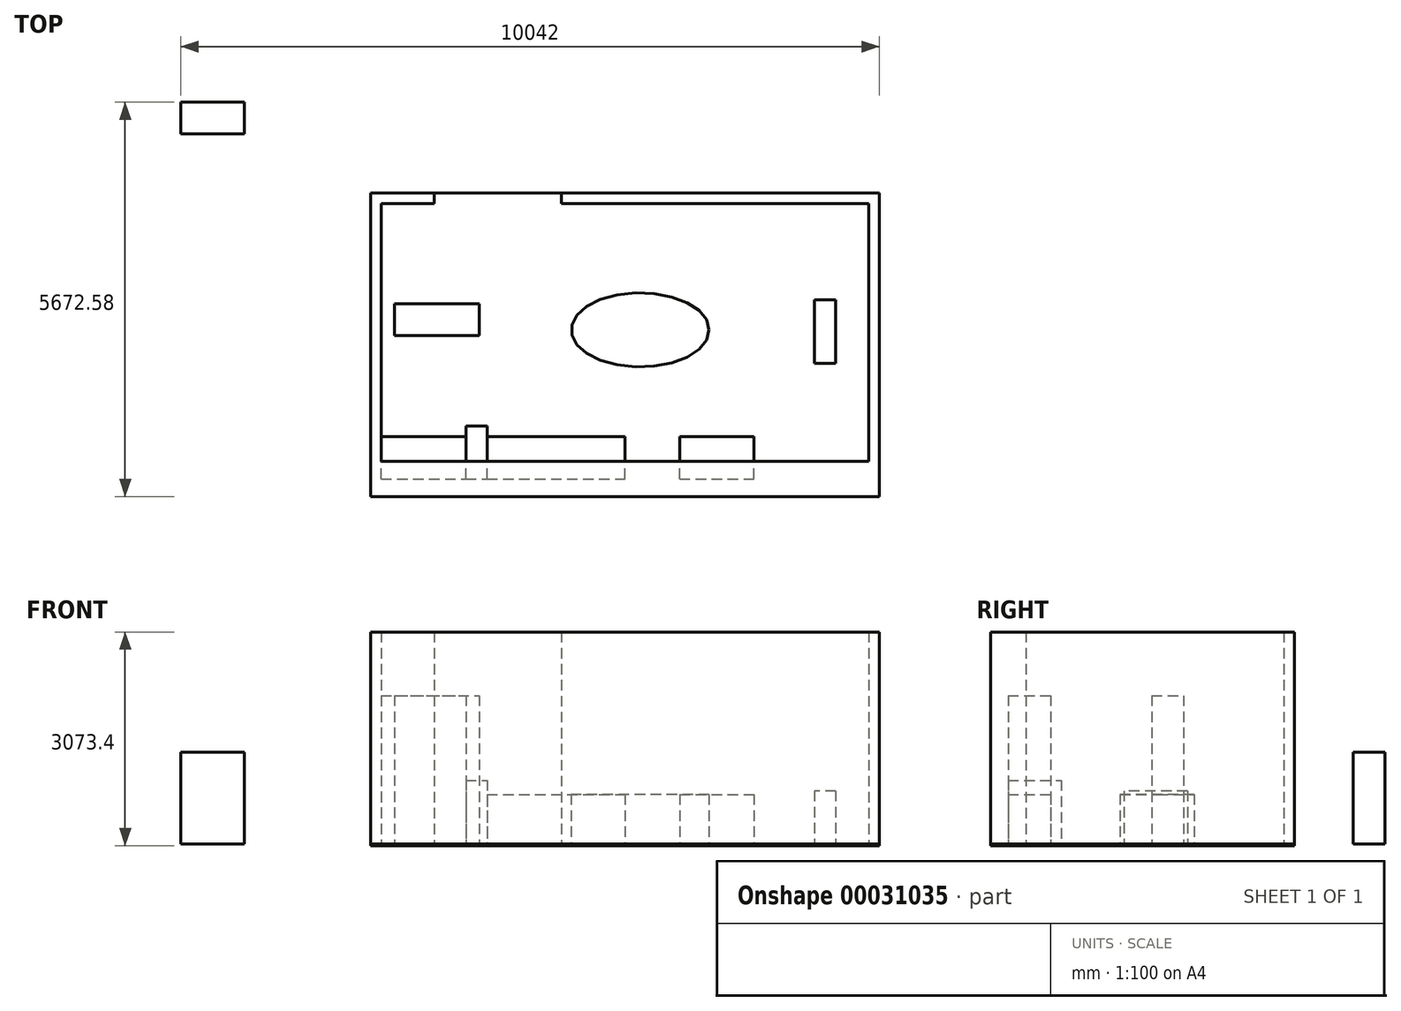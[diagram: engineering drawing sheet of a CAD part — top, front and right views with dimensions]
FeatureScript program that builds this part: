
annotation { "Feature Type Name" : "Feature", "Feature Type Description" : "" }
export const myFeature = defineFeature(function(context is Context, id is Id, definition is map)
    precondition{}
    {
        {
            var Q0;
            Q0=qCreatedBy(makeId("Top.planeOp"),FACE);
            var sketch = newSketch(context, id + "F0", { "sketchPlane" : qUnion([Q0])});
            skLineSegment(sketch, "E0.bottom", {"start": v(0, 0) * mm, "end": v(7010.4, 0) * mm, "construction": true});
            skLineSegment(sketch, "E0.top", {"start": v(0, 3962.4) * mm, "end": v(762, 3962.4) * mm});
            skLineSegment(sketch, "E0.left", {"start": v(0, 254) * mm, "end": v(0, 3962.4) * mm});
            skLineSegment(sketch, "E0.right", {"start": v(7010.4, 254) * mm, "end": v(7010.4, 3962.4) * mm});
            skLineSegment(sketch, "E1.bottom", {"start": v(-152.4, -254) * mm, "end": v(7162.8, -254) * mm});
            skLineSegment(sketch, "E1.top", {"start": v(-152.4, 4114.8) * mm, "end": v(762, 4114.8) * mm});
            skLineSegment(sketch, "E1.left", {"start": v(-152.4, -254) * mm, "end": v(-152.4, 4114.8) * mm});
            skLineSegment(sketch, "E1.right", {"start": v(7162.8, -254) * mm, "end": v(7162.8, 4114.8) * mm});
            skLineSegment(sketch, "E2.left", {"start": v(762, 3962.4) * mm, "end": v(762, 4114.8) * mm});
            skLineSegment(sketch, "E2.right", {"start": v(2590.8, 3962.4) * mm, "end": v(2590.8, 4114.8) * mm});
            skLineSegment(sketch, "E3.trimOffspring", {"start": v(2590.8, 3962.4) * mm, "end": v(7010.4, 3962.4) * mm});
            skLineSegment(sketch, "E4.trimOffspring", {"start": v(2590.8, 4114.8) * mm, "end": v(7162.8, 4114.8) * mm});
            skLineSegment(sketch, "E5", {"start": v(0, 254) * mm, "end": v(7010.4, 254) * mm});
            skSolve(sketch);
        }
        {
            var Q0;
            Q0 = qSketchRegion(id + "F0", true);
            extrude(context, id + "F1", {"entities" : qUnion([Q0]), "depth" : 3048 * mm});
        }
        {
            var Q0;
            Q0=makeQuery(id+"F1.opExtrude","CAP_FACE",FACE,{"disambiguationData":[OSD([sQuery(id+"F0.wireOp",EDGE,"E0.bottom"),sQuery(id+"F0.wireOp",EDGE,"E0.top"),sQuery(id+"F0.wireOp",EDGE,"E0.left"),sQuery(id+"F0.wireOp",EDGE,"E0.right"),sQuery(id+"F0.wireOp",EDGE,"E1.bottom"),sQuery(id+"F0.wireOp",EDGE,"E1.top"),sQuery(id+"F0.wireOp",EDGE,"E1.left"),sQuery(id+"F0.wireOp",EDGE,"E1.right"),sQuery(id+"F0.wireOp",EDGE,"E2.left"),sQuery(id+"F0.wireOp",EDGE,"E2.right"),sQuery(id+"F0.wireOp",EDGE,"E3.trimOffspring"),sQuery(id+"F0.wireOp",EDGE,"E4.trimOffspring")])],"isStart":true});
            var sketch = newSketch(context, id + "F2", { "sketchPlane" : qUnion([Q0])});
            skLineSegment(sketch, "E6.bottom", {"start": v(-152.4, 254) * mm, "end": v(7162.8, 254) * mm});
            skLineSegment(sketch, "E6.top", {"start": v(-152.4, -4114.8) * mm, "end": v(7162.8, -4114.8) * mm});
            skLineSegment(sketch, "E6.left", {"start": v(-152.4, 254) * mm, "end": v(-152.4, -4114.8) * mm});
            skLineSegment(sketch, "E6.right", {"start": v(7162.8, 254) * mm, "end": v(7162.8, -4114.8) * mm});
            skSolve(sketch);
        }
        {
            var Q0;
            Q0 = qSketchRegion(id + "F2", true);
            extrude(context, id + "F3", {"entities" : qUnion([Q0]), "depth" : 25.4 * mm});
        }
        {
            var Q0;
            Q0=makeQuery(id+"F3.opExtrude","CAP_FACE",FACE,{"disambiguationData":[OSD([sQuery(id+"F2.wireOp",EDGE,"E6.bottom"),sQuery(id+"F2.wireOp",EDGE,"E6.top"),sQuery(id+"F2.wireOp",EDGE,"E6.left"),sQuery(id+"F2.wireOp",EDGE,"E6.right")])],"isStart":true});
            var sketch = newSketch(context, id + "F4", { "sketchPlane" : qUnion([Q0])});
            skLineSegment(sketch, "E7.bottom", {"start": v(0, 0) * mm, "end": v(1219.2, 0) * mm});
            skLineSegment(sketch, "E7.top", {"start": v(0, 609.6) * mm, "end": v(1219.2, 609.6) * mm});
            skLineSegment(sketch, "E7.left", {"start": v(0, 0) * mm, "end": v(0, 609.6) * mm});
            skLineSegment(sketch, "E7.right", {"start": v(1219.2, 0) * mm, "end": v(1219.2, 609.6) * mm});
            skSolve(sketch);
        }
        {
            var Q0;
            Q0 = qSketchRegion(id + "F4", true);
            extrude(context, id + "F5", {"entities" : qUnion([Q0]), "depth" : 2133.6 * mm});
        }
        {
            var Q0;
            Q0=makeQuery(id+"F3.opExtrude","CAP_FACE",FACE,{"disambiguationData":[OSD([sQuery(id+"F2.wireOp",EDGE,"E6.bottom"),sQuery(id+"F2.wireOp",EDGE,"E6.top"),sQuery(id+"F2.wireOp",EDGE,"E6.left"),sQuery(id+"F2.wireOp",EDGE,"E6.right")])],"isStart":true});
            var sketch = newSketch(context, id + "F6", { "sketchPlane" : qUnion([Q0])});
            skLineSegment(sketch, "E8.bottom", {"start": v(1219.2, 0) * mm, "end": v(1524, 0) * mm});
            skLineSegment(sketch, "E8.top", {"start": v(1219.2, 762) * mm, "end": v(1524, 762) * mm});
            skLineSegment(sketch, "E8.left", {"start": v(1219.2, 0) * mm, "end": v(1219.2, 762) * mm});
            skLineSegment(sketch, "E8.right", {"start": v(1524, 0) * mm, "end": v(1524, 762) * mm});
            skSolve(sketch);
        }
        {
            var Q0;
            Q0 = qSketchRegion(id + "F6", true);
            extrude(context, id + "F7", {"entities" : qUnion([Q0]), "depth" : 914.4 * mm});
        }
        {
            var Q0;
            Q0=makeQuery(id+"F3.opExtrude","CAP_FACE",FACE,{"disambiguationData":[OSD([sQuery(id+"F2.wireOp",EDGE,"E6.bottom"),sQuery(id+"F2.wireOp",EDGE,"E6.top"),sQuery(id+"F2.wireOp",EDGE,"E6.left"),sQuery(id+"F2.wireOp",EDGE,"E6.right")])],"isStart":true});
            var sketch = newSketch(context, id + "F8", { "sketchPlane" : qUnion([Q0])});
            skLineSegment(sketch, "E9.bottom", {"start": v(1524, 0) * mm, "end": v(3505.2, 0) * mm});
            skLineSegment(sketch, "E9.top", {"start": v(1524, 609.6) * mm, "end": v(3505.2, 609.6) * mm});
            skLineSegment(sketch, "E9.left", {"start": v(1524, 0) * mm, "end": v(1524, 609.6) * mm});
            skLineSegment(sketch, "E9.right", {"start": v(3505.2, 0) * mm, "end": v(3505.2, 609.6) * mm});
            skSolve(sketch);
        }
        {
            var Q0;
            Q0 = qSketchRegion(id + "F8", true);
            extrude(context, id + "F9", {"entities" : qUnion([Q0]), "depth" : 711.2 * mm});
        }
        {
            var Q0;
            Q0=makeQuery(id+"F3.opExtrude","CAP_FACE",FACE,{"disambiguationData":[OSD([sQuery(id+"F2.wireOp",EDGE,"E6.bottom"),sQuery(id+"F2.wireOp",EDGE,"E6.top"),sQuery(id+"F2.wireOp",EDGE,"E6.left"),sQuery(id+"F2.wireOp",EDGE,"E6.right")])],"isStart":true});
            var sketch = newSketch(context, id + "F10", { "sketchPlane" : qUnion([Q0])});
            skLineSegment(sketch, "E10.bottom", {"start": v(-2879.24, 5418.58) * mm, "end": v(-1964.84, 5418.58) * mm});
            skLineSegment(sketch, "E10.top", {"start": v(-2879.24, 4961.38) * mm, "end": v(-1964.84, 4961.38) * mm});
            skLineSegment(sketch, "E10.left", {"start": v(-2879.24, 5418.58) * mm, "end": v(-2879.24, 4961.38) * mm});
            skLineSegment(sketch, "E10.right", {"start": v(-1964.84, 5418.58) * mm, "end": v(-1964.84, 4961.38) * mm});
            skSolve(sketch);
        }
        {
            var Q0;
            Q0 = qSketchRegion(id + "F10", true);
            extrude(context, id + "F11", {"entities" : qUnion([Q0]), "depth" : 1320.8 * mm});
        }
        {
            var Q0;
            Q0=makeQuery(id+"F3.opExtrude","CAP_FACE",FACE,{"disambiguationData":[OSD([sQuery(id+"F2.wireOp",EDGE,"E6.bottom"),sQuery(id+"F2.wireOp",EDGE,"E6.top"),sQuery(id+"F2.wireOp",EDGE,"E6.left"),sQuery(id+"F2.wireOp",EDGE,"E6.right")])],"isStart":true});
            var sketch = newSketch(context, id + "F12", { "sketchPlane" : qUnion([Q0])});
            skLineSegment(sketch, "E11.bottom", {"start": v(189.57, 2064.13) * mm, "end": v(1408.77, 2064.13) * mm});
            skLineSegment(sketch, "E11.top", {"start": v(189.57, 2521.33) * mm, "end": v(1408.77, 2521.33) * mm});
            skLineSegment(sketch, "E11.left", {"start": v(189.57, 2064.13) * mm, "end": v(189.57, 2521.33) * mm});
            skLineSegment(sketch, "E11.right", {"start": v(1408.77, 2064.13) * mm, "end": v(1408.77, 2521.33) * mm});
            skSolve(sketch);
        }
        {
            var Q0;
            Q0 = qSketchRegion(id + "F12", true);
            extrude(context, id + "F13", {"entities" : qUnion([Q0]), "depth" : 2133.6 * mm});
        }
        {
            var Q0;
            Q0=makeQuery(id+"F3.opExtrude","CAP_FACE",FACE,{"disambiguationData":[OSD([sQuery(id+"F2.wireOp",EDGE,"E6.bottom"),sQuery(id+"F2.wireOp",EDGE,"E6.top"),sQuery(id+"F2.wireOp",EDGE,"E6.left"),sQuery(id+"F2.wireOp",EDGE,"E6.right")])],"isStart":true});
            var sketch = newSketch(context, id + "F14", { "sketchPlane" : qUnion([Q0])});
            skLineSegment(sketch, "E12.bottom", {"start": v(4292.34, 0) * mm, "end": v(5359.14, 0) * mm});
            skLineSegment(sketch, "E12.top", {"start": v(4292.34, 609.6) * mm, "end": v(5359.14, 609.6) * mm});
            skLineSegment(sketch, "E12.left", {"start": v(4292.34, 0) * mm, "end": v(4292.34, 609.6) * mm});
            skLineSegment(sketch, "E12.right", {"start": v(5359.14, 0) * mm, "end": v(5359.14, 609.6) * mm});
            skSolve(sketch);
        }
        {
            var Q0;
            Q0 = qSketchRegion(id + "F14", true);
            extrude(context, id + "F15", {"entities" : qUnion([Q0]), "depth" : 711.2 * mm});
        }
        {
            var Q0;
            Q0=makeQuery(id+"F3.opExtrude","CAP_FACE",FACE,{"disambiguationData":[OSD([sQuery(id+"F2.wireOp",EDGE,"E6.bottom"),sQuery(id+"F2.wireOp",EDGE,"E6.top"),sQuery(id+"F2.wireOp",EDGE,"E6.left"),sQuery(id+"F2.wireOp",EDGE,"E6.right")])],"isStart":true});
            var sketch = newSketch(context, id + "F16", { "sketchPlane" : qUnion([Q0])});
            skLineSegment(sketch, "E13.bottom", {"start": v(6536.67, 2578.38) * mm, "end": v(6231.87, 2578.38) * mm});
            skLineSegment(sketch, "E13.top", {"start": v(6536.67, 1663.98) * mm, "end": v(6231.87, 1663.98) * mm});
            skLineSegment(sketch, "E13.left", {"start": v(6536.67, 2578.38) * mm, "end": v(6536.67, 1663.98) * mm});
            skLineSegment(sketch, "E13.right", {"start": v(6231.87, 2578.38) * mm, "end": v(6231.87, 1663.98) * mm});
            skSolve(sketch);
        }
        {
            var Q0;
            Q0 = qSketchRegion(id + "F16", true);
            extrude(context, id + "F17", {"entities" : qUnion([Q0]), "depth" : 762 * mm});
        }
        {
            var Q0;
            Q0=makeQuery(id+"F3.opExtrude","CAP_FACE",FACE,{"disambiguationData":[OSD([sQuery(id+"F2.wireOp",EDGE,"E6.bottom"),sQuery(id+"F2.wireOp",EDGE,"E6.top"),sQuery(id+"F2.wireOp",EDGE,"E6.left"),sQuery(id+"F2.wireOp",EDGE,"E6.right")])],"isStart":true});
            var sketch = newSketch(context, id + "F18", { "sketchPlane" : qUnion([Q0])});
            skEllipse(sketch, "E14", {"center": v(3725.3, 2143.4) * mm, "majorRadius": 990.6 * mm, "minorRadius": 533.4 * mm, "majorAxis": v(1, 0)});
            skPoint(sketch, "E15", {"position": v(3725.3, 2676.8) * mm});
            skPoint(sketch, "E16", {"position": v(3725.3, 1610) * mm});
            skPoint(sketch, "E17", {"position": v(4715.9, 2143.4) * mm});
            skPoint(sketch, "E18", {"position": v(2734.7, 2143.4) * mm});
            skSolve(sketch);
        }
        {
            var Q0;
            Q0 = qSketchRegion(id + "F18", true);
            extrude(context, id + "F19", {"entities" : qUnion([Q0]), "depth" : 711.2 * mm});
        }
    });
